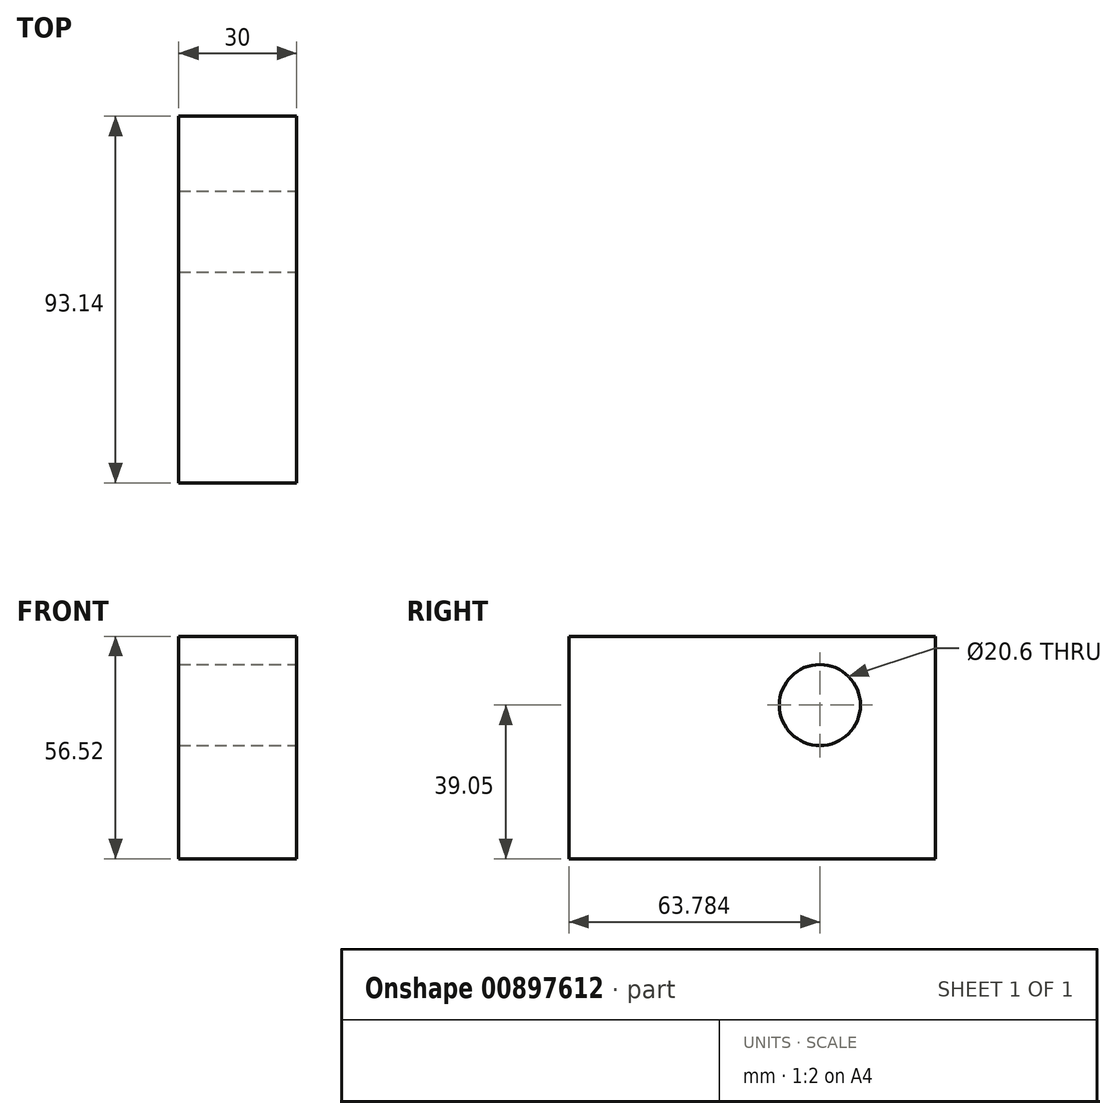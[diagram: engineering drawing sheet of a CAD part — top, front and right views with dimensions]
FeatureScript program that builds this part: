
annotation { "Feature Type Name" : "Feature", "Feature Type Description" : "" }
export const myFeature = defineFeature(function(context is Context, id is Id, definition is map)
    precondition{}
    {
        {
            var Q0;
            Q0=qCreatedBy(makeId("Right.planeOp"),FACE);
            var sketch = newSketch(context, id + "F0", { "sketchPlane" : qUnion([Q0])});
            skLineSegment(sketch, "E0.bottom", {"start": v(-14.96, 28.26) * mm, "end": v(78.18, 28.26) * mm});
            skLineSegment(sketch, "E0.top", {"start": v(-14.96, -28.26) * mm, "end": v(78.18, -28.26) * mm});
            skLineSegment(sketch, "E0.left", {"start": v(-14.96, 28.26) * mm, "end": v(-14.96, -28.26) * mm});
            skLineSegment(sketch, "E0.right", {"start": v(78.18, 28.26) * mm, "end": v(78.18, -28.26) * mm});
            skPoint(sketch, "E0.middle", {"position": v(31.6, 0) * mm});
            skSolve(sketch);
        }
        {
            var Q0;
            Q0=makeQuery(id+"F0.imprint","IMPRINT",FACE,{"disambiguationData":[TD([[makeQuery(id+"F0.imprint","IMPRINT",EDGE,{"derivedFrom":sQuery(id+"F0.wireOp",EDGE,"E0.bottom")}),-1.0]])]});
            extrude(context, id + "F1", {"entities" : qUnion([Q0]), "depth" : 30 * mm, "offsetDistance" : 25.4 * mm});
        }
        {
            var Q0;
            Q0=makeQuery(id+"F1.opExtrude","CAP_FACE",FACE,{"disambiguationData":[OSD([sQuery(id+"F0.wireOp",EDGE,"E0.bottom"),sQuery(id+"F0.wireOp",EDGE,"E0.top"),sQuery(id+"F0.wireOp",EDGE,"E0.left"),sQuery(id+"F0.wireOp",EDGE,"E0.right")])],"isStart":false});
            var sketch = newSketch(context, id + "F2", { "sketchPlane" : qUnion([Q0])});
            skCircle(sketch, "E1", {"center": v(48.82, 10.79) * mm, "radius": 10.3 * mm});
            skSolve(sketch);
        }
        {
            var Q0;
            Q0 = qSketchRegion(id + "F2", true);
            extrude(context, id + "F3", {"entities" : qUnion([Q0]), "operationType" : NewBodyOperationType.REMOVE, "oppositeDirection" : true, "depth" : 30 * mm, "offsetDistance" : 25.4 * mm});
        }
    });
